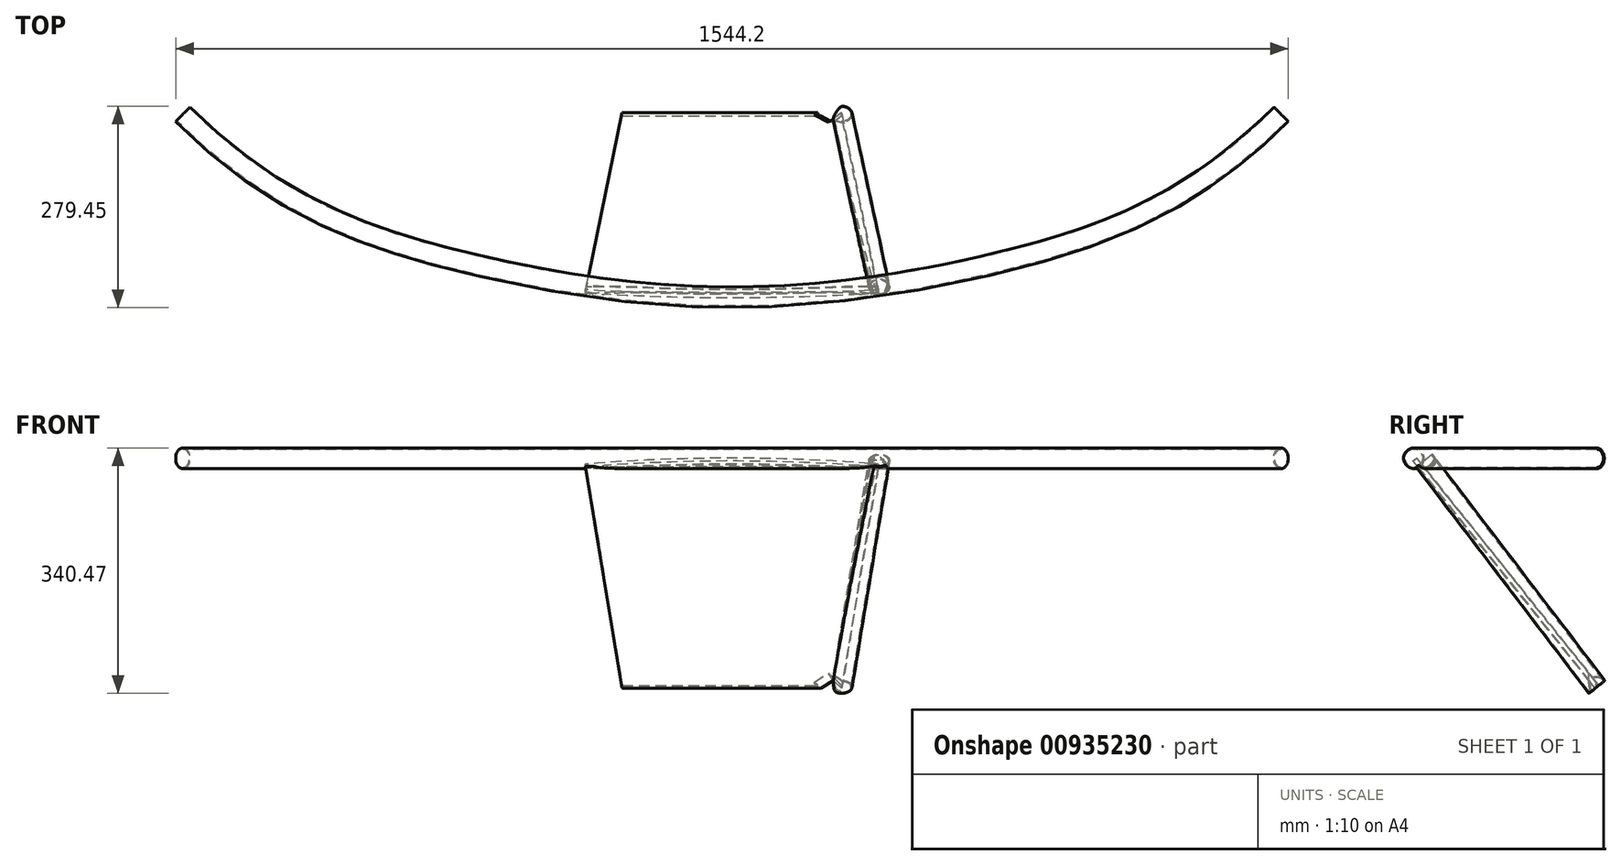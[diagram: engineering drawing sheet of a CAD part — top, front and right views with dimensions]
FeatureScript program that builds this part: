
annotation { "Feature Type Name" : "Feature", "Feature Type Description" : "" }
export const myFeature = defineFeature(function(context is Context, id is Id, definition is map)
    precondition{}
    {
        {
            var Q0;
            Q0=qCreatedBy(makeId("Right.planeOp"),FACE);
            var sketch = newSketch(context, id + "F0", { "sketchPlane" : qUnion([Q0])});
            skCircle(sketch, "E0", {"center": v(0, 0) * mm, "radius": 12.7 * mm});
            skCircle(sketch, "E1.0", {"center": v(0, 0) * mm, "radius": 14.29 * mm});
            skSolve(sketch);
        }
        {
            var Q0;
            Q0=qCreatedBy(makeId("Front.planeOp"),FACE);
            var sketch = newSketch(context, id + "F1", { "sketchPlane" : qUnion([Q0])});
            skLineSegment(sketch, "E2", {"start": v(-725.7, 0) * mm, "end": v(798.3, 0) * mm});
            skSolve(sketch);
        }
        {
            var Q0;
            Q0=qCreatedBy(makeId("Top.planeOp"),FACE);
            var sketch = newSketch(context, id + "F2", { "sketchPlane" : qUnion([Q0])});
            skFitSpline(sketch, "E3", {"points": [v(-762, 254) * mm, v(-381, 50.8) * mm, v(0, 0) * mm, v(381, 50.8) * mm, v(762, 254) * mm], "startDerivative": vector(1480.93, -1480.93) * mm, "endDerivative": vector(1480.93, 1480.93) * mm});
            skSolve(sketch);
        }
        {
            var Q0;
            Q0=makeQuery(id+"F0.imprint","IMPRINT",FACE,{"disambiguationData":[TD([[makeQuery(id+"F0.imprint","IMPRINT",EDGE,{"derivedFrom":sQuery(id+"F0.wireOp",EDGE,"E0")}),1.0]])]});
            var Q1;
            Q1=makeQuery(id+"F0.imprint","IMPRINT",FACE,{"disambiguationData":[TD([[makeQuery(id+"F0.imprint","IMPRINT",EDGE,{"derivedFrom":sQuery(id+"F0.wireOp",EDGE,"E0")}),-1.0]])]});
            var Q2;
            Q2=sQuery(id+"F0.wireOp",EDGE,"E0");
            var Q3;
            Q3=sQuery(id+"F0.wireOp",EDGE,"E1.0");
            var Q4;
            Q4=sQuery(id+"F2.wireOp",EDGE,"E3");
            sweep(context, id + "F3", {"profiles" : qUnion([Q0, Q1]), "surfaceProfiles" : qUnion([Q2, Q3]), "path" : qUnion([Q4])});
        }
        {
            var Q0;
            Q0=makeQuery(id+"F0.imprint","IMPRINT",FACE,{"disambiguationData":[TD([[makeQuery(id+"F0.imprint","IMPRINT",EDGE,{"derivedFrom":sQuery(id+"F0.wireOp",EDGE,"E0")}),1.0]])]});
            var Q1;
            Q1=sQuery(id+"F2.wireOp",EDGE,"E3");
            sweep(context, id + "F4", {"operationType" : NewBodyOperationType.REMOVE, "profiles" : qUnion([Q0]), "path" : qUnion([Q1])});
        }
        {
            var Q0;
            Q0=qCreatedBy(makeId("Right.planeOp"),FACE);
            var sketch = newSketch(context, id + "F5", { "sketchPlane" : qUnion([Q0])});
            skLineSegment(sketch, "E4", {"start": v(0, 0) * mm, "end": v(254, -317.25) * mm});
            skSolve(sketch);
        }
        {
            var Q0;
            Q0=qCreatedBy(makeId("Right.planeOp"),FACE);
            cPlane(context, id + "F6", {"entities" : qUnion([Q0]), "cplaneType" : CPlaneType.OFFSET, "offset" : 304.8 * mm, "width" : 152.4 * mm, "height" : 152.4 * mm});
        }
        {
            var Q0;
            Q0=qCreatedBy(id+"F6.planeOp",FACE);
            var sketch = newSketch(context, id + "F7", { "sketchPlane" : qUnion([Q0])});
            skLineSegment(sketch, "E5", {"start": v(0, 0) * mm, "end": v(254, -317.25) * mm});
            skSolve(sketch);
        }
        {
            var Q0;
            Q0=qCreatedBy(makeId("Right.planeOp"),FACE);
            cPlane(context, id + "F8", {"entities" : qUnion([Q0]), "cplaneType" : CPlaneType.OFFSET, "offset" : 304.8 * mm, "oppositeDirection" : true, "width" : 152.4 * mm, "height" : 152.4 * mm});
        }
        {
            var Q0;
            Q0=qCreatedBy(id+"F8.planeOp",FACE);
            var sketch = newSketch(context, id + "F9", { "sketchPlane" : qUnion([Q0])});
            skLineSegment(sketch, "E6", {"start": v(0, 0) * mm, "end": v(254, -317.25) * mm});
            skSolve(sketch);
        }
        {
            var Q0;
            Q0=sQuery(id+"F7.wireOp",VERTEX,"E5.start");
            var Q1;
            Q1=sQuery(id+"F7.wireOp",VERTEX,"E5.end");
            var Q2;
            Q2=sQuery(id+"F9.wireOp",VERTEX,"E6.start");
            cPlane(context, id + "F10", {"entities" : qUnion([Q0, Q1, Q2]), "cplaneType" : CPlaneType.THREE_POINT, "offset" : 25.4 * mm, "width" : 152.4 * mm, "height" : 152.4 * mm});
        }
        {
            var Q0;
            Q0=qCreatedBy(id+"F10.planeOp",FACE);
            var sketch = newSketch(context, id + "F11", { "sketchPlane" : qUnion([Q0])});
            skLineSegment(sketch, "E7.top", {"start": v(-152.4, -406.4) * mm, "end": v(152.4, -406.4) * mm});
            skArc(sketch, "E8", {"start": v(203.2, -12.7) * mm, "mid": v(0, -2.26) * mm, "end": v(-203.2, -12.7) * mm});
            skLineSegment(sketch, "E9", {"start": v(-203.2, -12.7) * mm, "end": v(-152.4, -406.4) * mm});
            skLineSegment(sketch, "E10", {"start": v(203.2, -12.7) * mm, "end": v(152.4, -406.4) * mm});
            skSolve(sketch);
        }
        {
            var Q0;
            Q0 = qSketchRegion(id + "F11", true);
            extrude(context, id + "F12", {"entities" : qUnion([Q0]), "operationType" : NewBodyOperationType.ADD, "endBound" : BoundingType.SYMMETRIC, "depth" : 6.35 * mm, "offsetDistance" : 25.4 * mm});
        }
        {
            var Q0;
            {var subQ0=sQuery(id+"F11.wireOp",EDGE,"E7.top");var subQ1=sQuery(id+"F11.wireOp",EDGE,"E10");Q0=makeQuery(id+"F12.boolean.opBoolean","SPLIT",EDGE,{"disambiguationData":[TD([makeQuery(id+"F12.opExtrude","SWEPT_FACE",FACE,{"disambiguationData":[OSD([subQ0])]})])],"derivedFrom":makeQuery(id+"F12.opExtrude","CAP_EDGE",EDGE,{"disambiguationData":[OSD([subQ1])],"isStart":true})});}
            cPlane(context, id + "F13", {"entities" : qUnion([Q0]), "cplaneType" : CPlaneType.LINE_ANGLE, "offset" : 25.4 * mm, "angle" : 0 * degree, "width" : 152.4 * mm, "height" : 152.4 * mm});
        }
        {
            var Q0;
            Q0=qCreatedBy(id+"F13.planeOp",FACE);
            var sketch = newSketch(context, id + "F14", { "sketchPlane" : qUnion([Q0])});
            skLineSegment(sketch, "E11", {"start": v(-254, -288.15) * mm, "end": v(-14.34, 30.19) * mm});
            skSolve(sketch);
        }
        {
            var Q0;
            Q0=makeQuery(id+"F12.opExtrude","SWEPT_FACE",FACE,{"disambiguationData":[OSD([sQuery(id+"F11.wireOp",EDGE,"E7.top")])]});
            var sketch = newSketch(context, id + "F15", { "sketchPlane" : qUnion([Q0])});
            skCircle(sketch, "E12", {"center": v(152.4, 0) * mm, "radius": 12.7 * mm});
            skCircle(sketch, "E13.0", {"center": v(152.4, 0) * mm, "radius": 14.3 * mm});
            skSolve(sketch);
        }
        {
            var Q0;
            Q0 = qSketchRegion(id + "F15", true);
            var Q1;
            Q1 = qConstructionFilter(qBodyType(qCreatedBy(id + "F14" ,EDGE), BodyType.WIRE), ConstructionObject.NO);
            sweep(context, id + "F16", {"operationType" : NewBodyOperationType.ADD, "profiles" : qUnion([Q0]), "path" : qUnion([Q1])});
        }
        {
            var Q0;
            Q0=makeQuery(id+"F12.opExtrude","SWEPT_EDGE",EDGE,{"disambiguationData":[OSD([sQuery(id+"F11.wireOp",EDGE,"E7.top"),sQuery(id+"F11.wireOp",EDGE,"E10")])]});
            cPlane(context, id + "F17", {"entities" : qUnion([Q0]), "cplaneType" : CPlaneType.LINE_ANGLE, "offset" : 25.4 * mm, "angle" : 50 * degree, "width" : 152.4 * mm, "height" : 152.4 * mm});
        }
        {
            var Q0;
            Q0=qCreatedBy(id+"F17.planeOp",FACE);
            var sketch = newSketch(context, id + "F18", { "sketchPlane" : qUnion([Q0])});
            skLineSegment(sketch, "E14.bottom", {"start": v(201.54, -370.44) * mm, "end": v(228.39, -370.44) * mm});
            skLineSegment(sketch, "E14.top", {"start": v(201.54, -319.76) * mm, "end": v(228.39, -319.76) * mm});
            skLineSegment(sketch, "E14.left", {"start": v(201.54, -370.44) * mm, "end": v(201.54, -319.76) * mm});
            skLineSegment(sketch, "E14.right", {"start": v(228.39, -370.44) * mm, "end": v(228.39, -319.76) * mm});
            skSolve(sketch);
        }
        {
            var Q0;
            Q0 = qSketchRegion(id + "F18", true);
            extrude(context, id + "F19", {"entities" : qUnion([Q0]), "operationType" : NewBodyOperationType.REMOVE, "oppositeDirection" : true, "depth" : 25.4 * mm, "offsetDistance" : 25.4 * mm});
        }
    });
